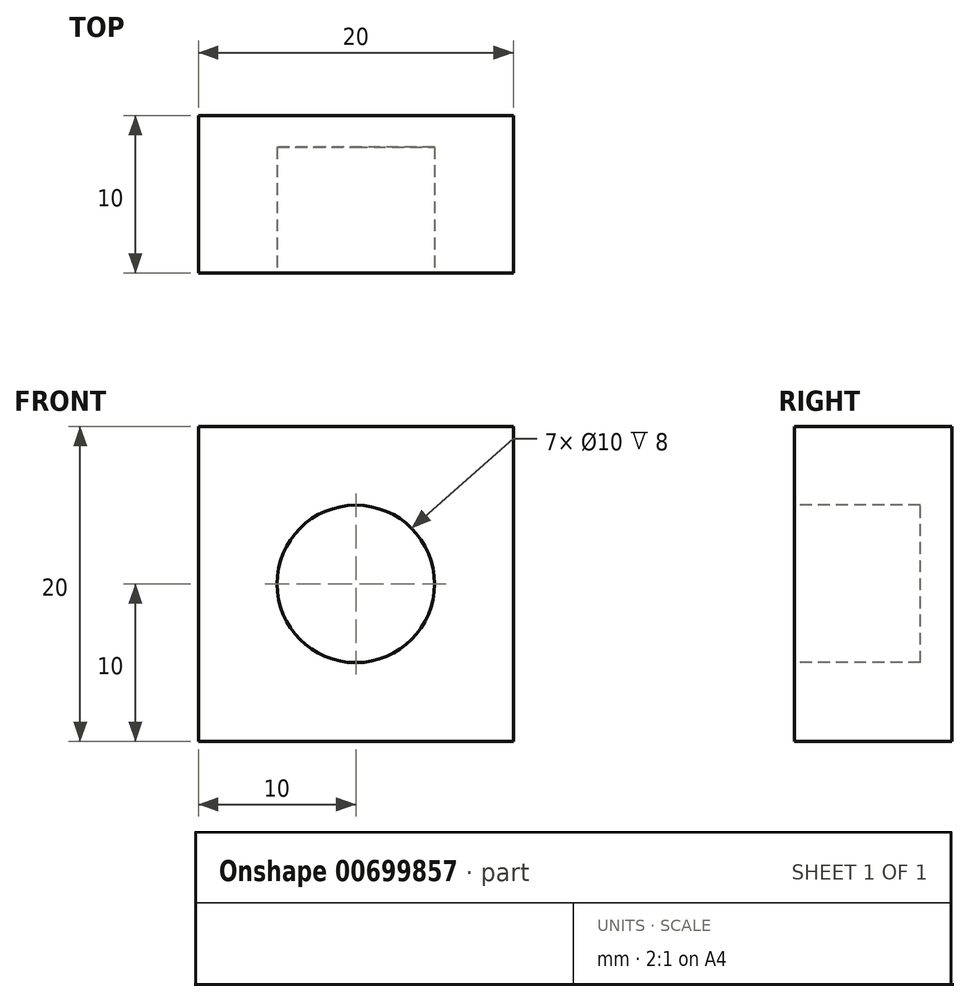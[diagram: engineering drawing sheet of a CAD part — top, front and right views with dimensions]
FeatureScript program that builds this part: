
annotation { "Feature Type Name" : "Feature", "Feature Type Description" : "" }
export const myFeature = defineFeature(function(context is Context, id is Id, definition is map)
    precondition{}
    {
        {
            var Q0;
            Q0=qCreatedBy(makeId("Front.planeOp"),FACE);
            var sketch = newSketch(context, id + "F0", { "sketchPlane" : qUnion([Q0])});
            skLineSegment(sketch, "E0.bottom", {"start": v(-10, 10) * mm, "end": v(10, 10) * mm});
            skLineSegment(sketch, "E0.top", {"start": v(-10, -10) * mm, "end": v(10, -10) * mm});
            skLineSegment(sketch, "E0.left", {"start": v(-10, 10) * mm, "end": v(-10, -10) * mm});
            skLineSegment(sketch, "E0.right", {"start": v(10, 10) * mm, "end": v(10, -10) * mm});
            skSolve(sketch);
        }
        {
            var Q0;
            Q0=makeQuery(id+"F0.imprint","IMPRINT",FACE,{"disambiguationData":[TD([[makeQuery(id+"F0.imprint","IMPRINT",EDGE,{"derivedFrom":sQuery(id+"F0.wireOp",EDGE,"E0.bottom")}),-1.0]])]});
            extrude(context, id + "F1", {"entities" : qUnion([Q0]), "endBound" : BoundingType.SYMMETRIC, "depth" : 10 * mm, "offsetDistance" : 25 * mm});
        }
        {
            var Q0;
            Q0=makeQuery(id+"F1.opExtrude","CAP_FACE",FACE,{"disambiguationData":[OSD([sQuery(id+"F0.wireOp",EDGE,"E0.bottom"),sQuery(id+"F0.wireOp",EDGE,"E0.top"),sQuery(id+"F0.wireOp",EDGE,"E0.left"),sQuery(id+"F0.wireOp",EDGE,"E0.right")])],"isStart":false});
            var sketch = newSketch(context, id + "F2", { "sketchPlane" : qUnion([Q0])});
            skCircle(sketch, "E1", {"center": v(0, 0) * mm, "radius": 5 * mm});
            skSolve(sketch);
        }
        {
            var Q0;
            Q0=makeQuery(id+"F2.imprint","IMPRINT",FACE,{"disambiguationData":[TD([[makeQuery(id+"F2.imprint","IMPRINT",EDGE,{"derivedFrom":sQuery(id+"F2.wireOp",EDGE,"E1")}),1.0]])]});
            extrude(context, id + "F3", {"entities" : qUnion([Q0]), "operationType" : NewBodyOperationType.REMOVE, "oppositeDirection" : true, "depth" : 8 * mm, "offsetDistance" : 25 * mm});
        }
    });
